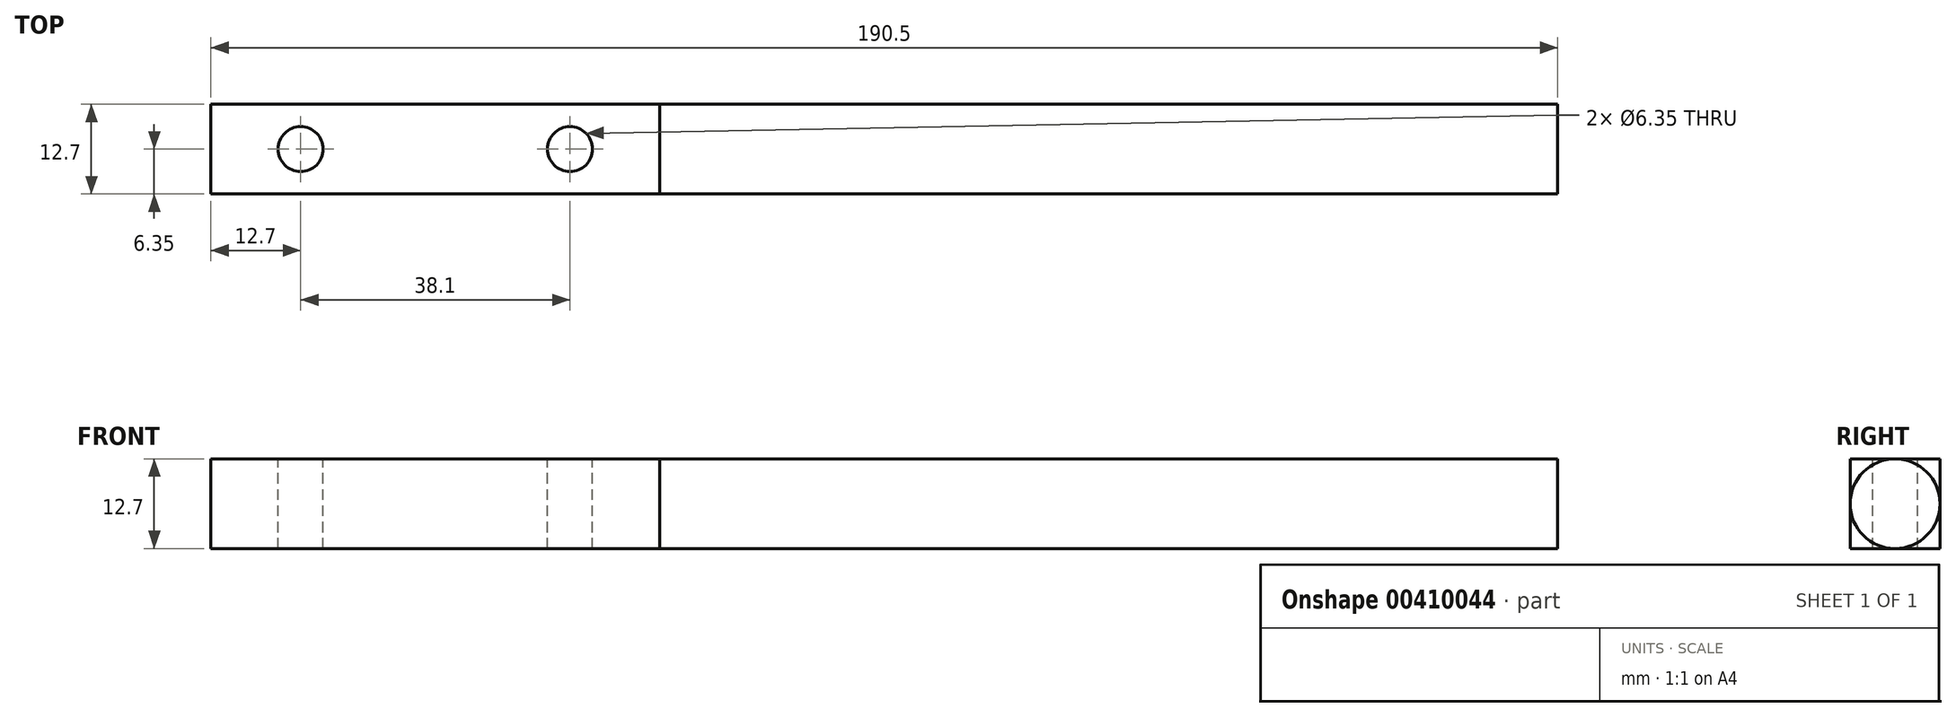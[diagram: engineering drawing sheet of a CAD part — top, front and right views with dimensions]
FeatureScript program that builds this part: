
annotation { "Feature Type Name" : "Feature", "Feature Type Description" : "" }
export const myFeature = defineFeature(function(context is Context, id is Id, definition is map)
    precondition{}
    {
        {
            var Q0;
            Q0=qCreatedBy(makeId("Right.planeOp"),FACE);
            var sketch = newSketch(context, id + "F0", { "sketchPlane" : qUnion([Q0])});
            skCircle(sketch, "E0", {"center": v(0, 0) * mm, "radius": 6.35 * mm});
            skSolve(sketch);
        }
        {
            var Q0;
            Q0 = qSketchRegion(id + "F0", true);
            extrude(context, id + "F1", {"entities" : qUnion([Q0]), "depth" : 127 * mm});
        }
        {
            var Q0;
            Q0=qCreatedBy(makeId("Right.planeOp"),FACE);
            var sketch = newSketch(context, id + "F2", { "sketchPlane" : qUnion([Q0])});
            skLineSegment(sketch, "E1.bottom", {"start": v(6.35, 6.35) * mm, "end": v(-6.35, 6.35) * mm});
            skLineSegment(sketch, "E1.top", {"start": v(6.35, -6.35) * mm, "end": v(-6.35, -6.35) * mm});
            skLineSegment(sketch, "E1.left", {"start": v(6.35, 6.35) * mm, "end": v(6.35, -6.35) * mm});
            skLineSegment(sketch, "E1.right", {"start": v(-6.35, 6.35) * mm, "end": v(-6.35, -6.35) * mm});
            skSolve(sketch);
        }
        {
            var Q0;
            Q0 = qSketchRegion(id + "F2", true);
            extrude(context, id + "F3", {"entities" : qUnion([Q0]), "operationType" : NewBodyOperationType.ADD, "oppositeDirection" : true, "depth" : 63.5 * mm});
        }
        {
            var Q0;
            Q0=makeQuery(id+"F3.opExtrude","SWEPT_FACE",FACE,{"disambiguationData":[OSD([sQuery(id+"F2.wireOp",EDGE,"E1.bottom")])]});
            var sketch = newSketch(context, id + "F4", { "sketchPlane" : qUnion([Q0])});
            skLineSegment(sketch, "E2", {"start": v(18.53, 0) * mm, "end": v(-87.82, 0) * mm, "construction": true});
            skLineSegment(sketch, "E3", {"start": v(-50.8, -25.93) * mm, "end": v(-50.8, 31.3) * mm, "construction": true});
            skCircle(sketch, "E4", {"center": v(-50.8, 0) * mm, "radius": 3.18 * mm});
            skCircle(sketch, "E5", {"center": v(-12.7, 0) * mm, "radius": 3.18 * mm});
            skSolve(sketch);
        }
        {
            var Q0;
            Q0 = qSketchRegion(id + "F4", true);
            extrude(context, id + "F5", {"entities" : qUnion([Q0]), "operationType" : NewBodyOperationType.REMOVE, "endBound" : BoundingType.THROUGH_ALL, "oppositeDirection" : true, "depth" : 25.4 * mm});
        }
    });
